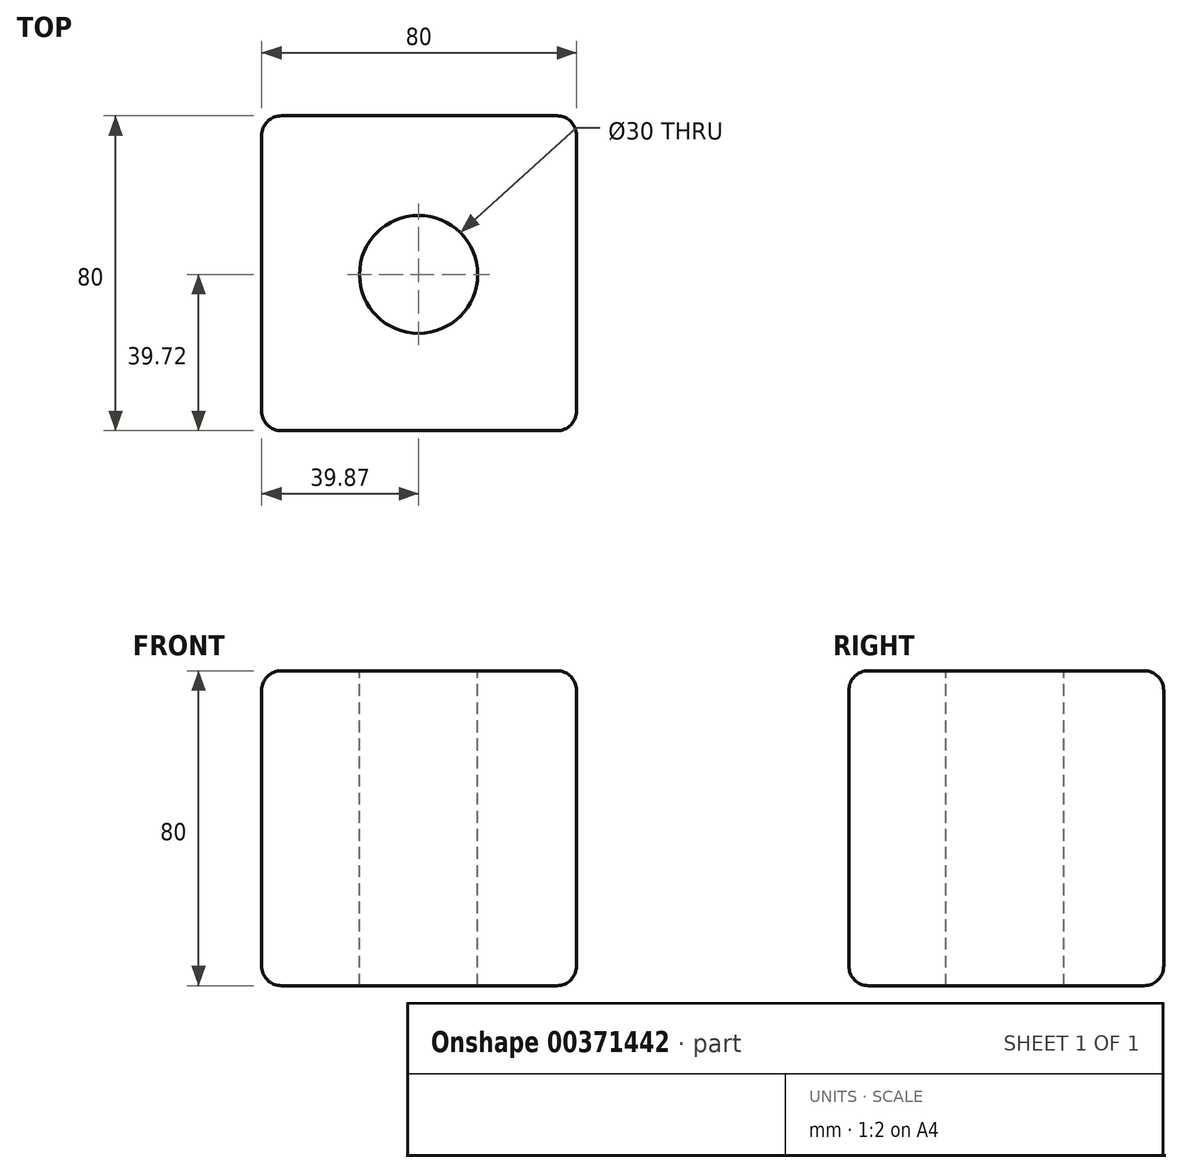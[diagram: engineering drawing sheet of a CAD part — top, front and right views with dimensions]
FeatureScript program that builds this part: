
annotation { "Feature Type Name" : "Feature", "Feature Type Description" : "" }
export const myFeature = defineFeature(function(context is Context, id is Id, definition is map)
    precondition{}
    {
        {
            var Q0;
            Q0=qCreatedBy(makeId("Top.planeOp"),FACE);
            var sketch = newSketch(context, id + "F0", { "sketchPlane" : qUnion([Q0])});
            skLineSegment(sketch, "E0.bottom", {"start": v(-55.17, 15.53) * mm, "end": v(24.83, 15.53) * mm});
            skLineSegment(sketch, "E0.top", {"start": v(-55.17, -64.47) * mm, "end": v(24.83, -64.47) * mm});
            skLineSegment(sketch, "E0.left", {"start": v(-55.17, 15.53) * mm, "end": v(-55.17, -64.47) * mm});
            skLineSegment(sketch, "E0.right", {"start": v(24.83, 15.53) * mm, "end": v(24.83, -64.47) * mm});
            skSolve(sketch);
        }
        {
            var Q0;
            Q0=makeQuery(id+"F0.imprint","IMPRINT",FACE,{"disambiguationData":[TD([[makeQuery(id+"F0.imprint","IMPRINT",EDGE,{"derivedFrom":sQuery(id+"F0.wireOp",EDGE,"E0.bottom")}),-1.0]])]});
            extrude(context, id + "F1", {"entities" : qUnion([Q0]), "depth" : 80 * mm});
        }
        {
            var Q0;
            Q0=makeQuery(id+"F1.opExtrude","CAP_FACE",FACE,{"disambiguationData":[OSD([sQuery(id+"F0.wireOp",EDGE,"E0.bottom"),sQuery(id+"F0.wireOp",EDGE,"E0.top"),sQuery(id+"F0.wireOp",EDGE,"E0.left"),sQuery(id+"F0.wireOp",EDGE,"E0.right")])],"isStart":false});
            var sketch = newSketch(context, id + "F2", { "sketchPlane" : qUnion([Q0])});
            skCircle(sketch, "E1", {"center": v(-15.3, -24.75) * mm, "radius": 15 * mm});
            skSolve(sketch);
        }
        {
            var Q0;
            Q0=makeQuery(id+"F2.imprint","IMPRINT",FACE,{"disambiguationData":[TD([[makeQuery(id+"F2.imprint","IMPRINT",EDGE,{"derivedFrom":sQuery(id+"F2.wireOp",EDGE,"E1")}),1.0]])]});
            extrude(context, id + "F3", {"entities" : qUnion([Q0]), "operationType" : NewBodyOperationType.REMOVE, "endBound" : BoundingType.THROUGH_ALL, "oppositeDirection" : true, "depth" : 25 * mm});
        }
        {
            var Q0;
            Q0=makeQuery(id+"F1.opExtrude","CAP_EDGE",EDGE,{"disambiguationData":[OSD([sQuery(id+"F0.wireOp",EDGE,"E0.bottom")])],"isStart":false});
            var Q1;
            Q1=makeQuery(id+"F1.opExtrude","CAP_EDGE",EDGE,{"disambiguationData":[OSD([sQuery(id+"F0.wireOp",EDGE,"E0.left")])],"isStart":false});
            var Q2;
            Q2=makeQuery(id+"F1.opExtrude","CAP_EDGE",EDGE,{"disambiguationData":[OSD([sQuery(id+"F0.wireOp",EDGE,"E0.top")])],"isStart":false});
            var Q3;
            Q3=makeQuery(id+"F1.opExtrude","CAP_EDGE",EDGE,{"disambiguationData":[OSD([sQuery(id+"F0.wireOp",EDGE,"E0.right")])],"isStart":false});
            var Q4;
            Q4=makeQuery(id+"F1.opExtrude","SWEPT_EDGE",EDGE,{"disambiguationData":[OSD([sQuery(id+"F0.wireOp",EDGE,"E0.bottom"),sQuery(id+"F0.wireOp",EDGE,"E0.right")])]});
            var Q5;
            Q5=makeQuery(id+"F1.opExtrude","SWEPT_FACE",FACE,{"disambiguationData":[OSD([sQuery(id+"F0.wireOp",EDGE,"E0.right")])]});
            var Q6;
            Q6=makeQuery(id+"F1.opExtrude","SWEPT_EDGE",EDGE,{"disambiguationData":[OSD([sQuery(id+"F0.wireOp",EDGE,"E0.top"),sQuery(id+"F0.wireOp",EDGE,"E0.right")])]});
            var Q7;
            Q7=makeQuery(id+"F1.opExtrude","SWEPT_FACE",FACE,{"disambiguationData":[OSD([sQuery(id+"F0.wireOp",EDGE,"E0.left")])]});
            var Q8;
            Q8=makeQuery(id+"F1.opExtrude","CAP_EDGE",EDGE,{"disambiguationData":[OSD([sQuery(id+"F0.wireOp",EDGE,"E0.bottom")])],"isStart":true});
            var Q9;
            Q9=makeQuery(id+"F1.opExtrude","CAP_EDGE",EDGE,{"disambiguationData":[OSD([sQuery(id+"F0.wireOp",EDGE,"E0.top")])],"isStart":true});
            fillet(context, id + "F4", {"entities" : qUnion([Q0, Q1, Q2, Q3, Q4, Q5, Q6, Q7, Q8, Q9]), "radius" : 5 * mm, "tangentPropagation" : true, "allowEdgeOverflow" : false});
        }
    });
